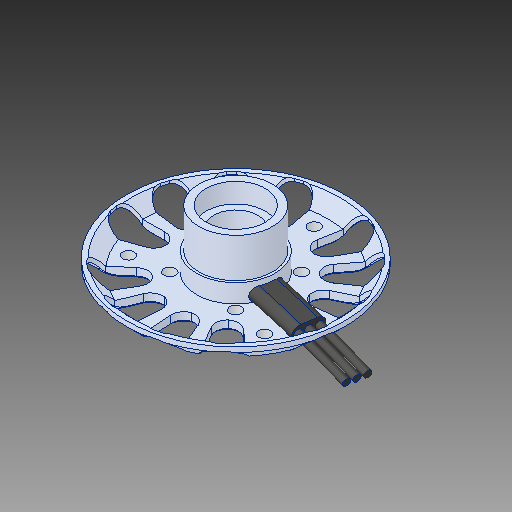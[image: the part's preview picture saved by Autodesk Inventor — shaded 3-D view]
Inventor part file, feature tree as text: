
AUTODESK INVENTOR PART (.ipt)
format: ipt  version: 2019.4 (Build 234330000, 330)  size: 931,328 bytes
history: mixed  units: mm
features: chamfer x1, other x1, imported_body x1
ambient origin geometry x8: Origin, YZ Plane, XZ Plane, XY Plane, X Axis, Y Axis, Z Axis, Center Point
bodies: Solid1 (imported_parasolid), Solid2 (imported_parasolid)
feature tree (3):
  chamfer  "Chamfer2"  [1 undecoded]
  other  "Flex1"
  imported_body  NMx_Import_Brep_tag  [imported B-rep: ~11 faces, bbox_mm=None]
note: 1 required parameter value undecoded (feature->parameter linkage not recoverable at this tier; creation-order binding heuristic only, values carry confidence <= 0.55)
